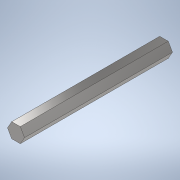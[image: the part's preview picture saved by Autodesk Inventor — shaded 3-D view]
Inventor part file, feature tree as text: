
AUTODESK INVENTOR PART (.ipt)
format: ipt  version: 2020 (Build 240168000, 168)  size: 100,352 bytes
history: native  units: in
note: dims shown in document units (in); Inventor stores cm internally (conversion verified against a paired STEP export)
features: extrude x1, sketch x1
ambient origin geometry x8: Origin, YZ Plane, XZ Plane, XY Plane, X Axis, Y Axis, Z Axis, Center Point
bodies: Solid1 (feature_tree)
feature tree (2):
  extrude  "Extrusion1"  Depth=5.0in TaperAngle=0.0deg
  sketch  "Sketch1"  dims[d0=0.5in d1=5.0in d2=0.0in]
